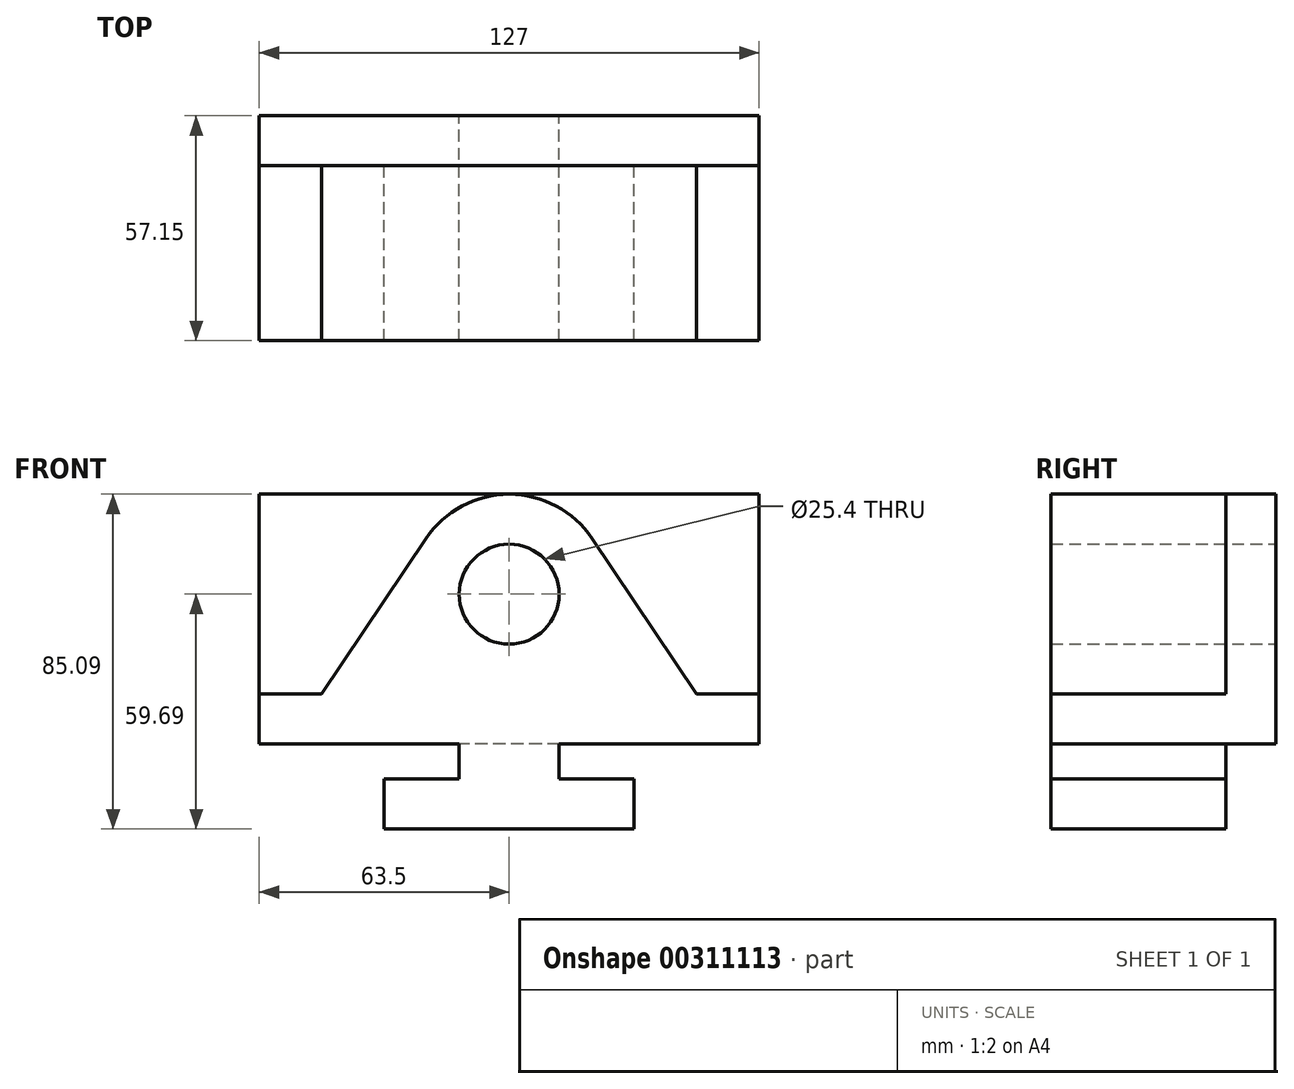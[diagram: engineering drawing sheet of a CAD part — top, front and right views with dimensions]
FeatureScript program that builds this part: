
annotation { "Feature Type Name" : "Feature", "Feature Type Description" : "" }
export const myFeature = defineFeature(function(context is Context, id is Id, definition is map)
    precondition{}
    {
        {
            var Q0;
            Q0=qCreatedBy(makeId("Front.planeOp"),FACE);
            var sketch = newSketch(context, id + "F0", { "sketchPlane" : qUnion([Q0])});
            skLineSegment(sketch, "E0", {"start": v(0, 0) * mm, "end": v(63.5, 0) * mm});
            skLineSegment(sketch, "E1", {"start": v(63.5, 0) * mm, "end": v(63.5, 12.7) * mm});
            skLineSegment(sketch, "E2", {"start": v(63.5, 12.7) * mm, "end": v(44.45, 12.7) * mm});
            skLineSegment(sketch, "E3", {"start": v(44.45, 12.7) * mm, "end": v(44.45, 21.59) * mm});
            skLineSegment(sketch, "E4", {"start": v(0, 0) * mm, "end": v(0, 12.7) * mm});
            skLineSegment(sketch, "E5", {"start": v(0, 12.7) * mm, "end": v(19.05, 12.7) * mm});
            skLineSegment(sketch, "E6", {"start": v(19.05, 12.7) * mm, "end": v(19.05, 21.59) * mm});
            skLineSegment(sketch, "E7", {"start": v(19.05, 21.59) * mm, "end": v(-31.75, 21.59) * mm});
            skLineSegment(sketch, "E8", {"start": v(44.45, 21.59) * mm, "end": v(95.25, 21.59) * mm});
            skLineSegment(sketch, "E9", {"start": v(95.25, 21.59) * mm, "end": v(95.25, 34.3) * mm});
            skLineSegment(sketch, "E10", {"start": v(-31.75, 21.59) * mm, "end": v(-31.75, 34.29) * mm});
            skLineSegment(sketch, "E11", {"start": v(-31.75, 34.3) * mm, "end": v(-15.88, 34.3) * mm});
            skLineSegment(sketch, "E12", {"start": v(95.25, 34.3) * mm, "end": v(79.38, 34.3) * mm});
            skLineSegment(sketch, "E13", {"start": v(-15.88, 34.29) * mm, "end": v(10.66, 73.84) * mm});
            skLineSegment(sketch, "E14", {"start": v(79.38, 34.29) * mm, "end": v(52.84, 73.84) * mm});
            skArc(sketch, "E15", {"start": v(52.84, 73.84) * mm, "mid": v(31.75, 85.1) * mm, "end": v(10.66, 73.84) * mm});
            skLineSegment(sketch, "E16", {"start": v(31.75, 85.1) * mm, "end": v(31.75, 59.7) * mm});
            skPoint(sketch, "E16.endSnap0", {"position": v(31.75, 85.1) * mm});
            skCircle(sketch, "E17", {"center": v(31.75, 59.7) * mm, "radius": 12.7 * mm});
            skSolve(sketch);
        }
        {
            var Q0;
            Q0 = qSketchRegion(id + "F0", true);
            extrude(context, id + "F1", {"entities" : qUnion([Q0]), "depth" : 44.45 * mm});
        }
        {
            var Q0;
            Q0=qCreatedBy(makeId("Right.planeOp"),FACE);
            var sketch = newSketch(context, id + "F2", { "sketchPlane" : qUnion([Q0])});
            skLineSegment(sketch, "E18", {"start": v(0, 0) * mm, "end": v(0, 21.59) * mm});
            skLineSegment(sketch, "E19", {"start": v(0, 21.59) * mm, "end": v(0, 85.1) * mm});
            skLineSegment(sketch, "E20", {"start": v(0, 85.1) * mm, "end": v(12.7, 85.1) * mm});
            skLineSegment(sketch, "E21", {"start": v(12.7, 85.1) * mm, "end": v(12.7, 21.59) * mm});
            skLineSegment(sketch, "E22", {"start": v(12.7, 21.59) * mm, "end": v(0, 21.59) * mm});
            skSolve(sketch);
        }
        {
            var Q0;
            Q0 = qSketchRegion(id + "F2", true);
            extrude(context, id + "F3", {"entities" : qUnion([Q0]), "operationType" : NewBodyOperationType.ADD, "depth" : 158.75 * mm});
        }
        {
            var Q0;
            {var subQ2=sQuery(id+"F2.wireOp",EDGE,"E19");var subQ3=makeQuery(id+"F3.opExtrude","SWEPT_FACE",FACE,{"disambiguationData":[OSD([subQ2])]});Q0=makeQuery(id+"F3.boolean.opBoolean","SPLIT",FACE,{"disambiguationData":[TD([makeQuery(id+"F1.opExtrude","SWEPT_FACE",FACE,{"disambiguationData":[OSD([sQuery(id+"F0.wireOp",EDGE,"E7")])]})])],"derivedFrom":subQ3});}
            var sketch = newSketch(context, id + "F4", { "sketchPlane" : qUnion([Q0])});
            skLineSegment(sketch, "E23", {"start": v(95.25, 21.59) * mm, "end": v(158.75, 21.59) * mm});
            skLineSegment(sketch, "E24", {"start": v(158.75, 21.59) * mm, "end": v(158.75, 85.1) * mm});
            skLineSegment(sketch, "E25", {"start": v(158.75, 85.1) * mm, "end": v(95.25, 85.1) * mm});
            skLineSegment(sketch, "E26", {"start": v(95.25, 85.1) * mm, "end": v(95.25, 21.59) * mm});
            skSolve(sketch);
        }
        {
            var Q0;
            Q0 = qSketchRegion(id + "F4", true);
            extrude(context, id + "F5", {"entities" : qUnion([Q0]), "operationType" : NewBodyOperationType.REMOVE, "oppositeDirection" : true, "depth" : 50.8 * mm});
        }
        {
            var Q0;
            Q0=makeQuery(id+"F3.opExtrude","CAP_FACE",FACE,{"disambiguationData":[OSD([sQuery(id+"F2.wireOp",EDGE,"E19"),sQuery(id+"F2.wireOp",EDGE,"E20"),sQuery(id+"F2.wireOp",EDGE,"E21"),sQuery(id+"F2.wireOp",EDGE,"E22")])],"isStart":true});
            var sketch = newSketch(context, id + "F6", { "sketchPlane" : qUnion([Q0])});
            skLineSegment(sketch, "E27", {"start": v(-12.7, 85.1) * mm, "end": v(0, 85.1) * mm});
            skLineSegment(sketch, "E28", {"start": v(0, 85.1) * mm, "end": v(0, 21.59) * mm});
            skLineSegment(sketch, "E29", {"start": v(0, 21.59) * mm, "end": v(-12.7, 21.59) * mm});
            skLineSegment(sketch, "E30", {"start": v(-12.7, 21.59) * mm, "end": v(-12.7, 85.1) * mm});
            skSolve(sketch);
        }
        {
            var Q0;
            Q0 = qSketchRegion(id + "F6", true);
            extrude(context, id + "F7", {"entities" : qUnion([Q0]), "operationType" : NewBodyOperationType.ADD, "depth" : 31.75 * mm});
        }
        {
            var Q0;
            Q0=makeQuery(id+"F3.boolean.opBoolean","SPLIT",FACE,{"disambiguationData":[TD([makeQuery(id+"F1.opExtrude","SWEPT_FACE",FACE,{"disambiguationData":[OSD([sQuery(id+"F0.wireOp",EDGE,"E17")])]})])],"derivedFrom":makeQuery(id+"F3.opExtrude","SWEPT_FACE",FACE,{"disambiguationData":[OSD([sQuery(id+"F2.wireOp",EDGE,"E19")])]})});
            var sketch = newSketch(context, id + "F8", { "sketchPlane" : qUnion([Q0])});
            skCircle(sketch, "E31", {"center": v(31.75, 59.7) * mm, "radius": 12.7 * mm});
            skSolve(sketch);
        }
        {
            var Q0;
            Q0 = qSketchRegion(id + "F8", true);
            extrude(context, id + "F9", {"entities" : qUnion([Q0]), "operationType" : NewBodyOperationType.REMOVE, "oppositeDirection" : true, "depth" : 25.4 * mm});
        }
    });
